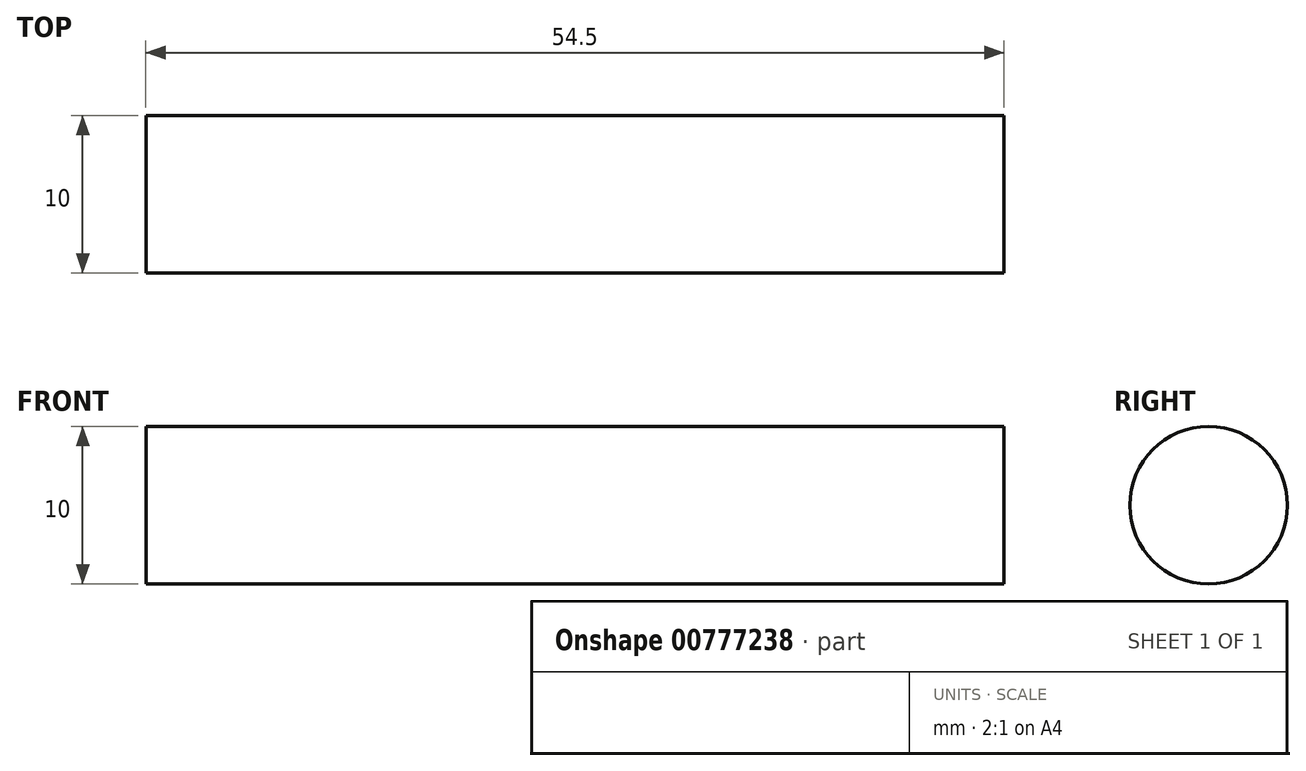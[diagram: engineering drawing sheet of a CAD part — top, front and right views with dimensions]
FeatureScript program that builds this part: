
annotation { "Feature Type Name" : "Feature", "Feature Type Description" : "" }
export const myFeature = defineFeature(function(context is Context, id is Id, definition is map)
    precondition{}
    {
        {
            var Q0;
            Q0=qCreatedBy(makeId("Front.planeOp"),FACE);
            var sketch = newSketch(context, id + "F0", { "sketchPlane" : qUnion([Q0])});
            skLineSegment(sketch, "E0.bottom", {"start": v(-27.25, 2.5) * mm, "end": v(27.25, 2.5) * mm});
            skLineSegment(sketch, "E0.top", {"start": v(-27.25, -2.5) * mm, "end": v(27.25, -2.5) * mm});
            skLineSegment(sketch, "E0.left", {"start": v(-27.25, 2.5) * mm, "end": v(-27.25, -2.5) * mm});
            skLineSegment(sketch, "E0.right", {"start": v(27.25, 2.5) * mm, "end": v(27.25, -2.5) * mm});
            skPoint(sketch, "E0.middle", {"position": v(0, 0) * mm});
            skSolve(sketch);
        }
        {
            var Q0;
            Q0=makeQuery(id+"F0.imprint","IMPRINT",FACE,{"disambiguationData":[TD([[makeQuery(id+"F0.imprint","IMPRINT",EDGE,{"derivedFrom":sQuery(id+"F0.wireOp",EDGE,"E0.bottom")}),-1.0]])]});
            var Q1;
            Q1=sQuery(id+"F0.wireOp",EDGE,"E0.top");
            revolve(context, id + "F1", {"surfaceOperationType" : NewSurfaceOperationType.NEW, "entities" : qUnion([Q0]), "axis" : qUnion([Q1]), "revolveType" : RevolveType.FULL});
        }
    });
